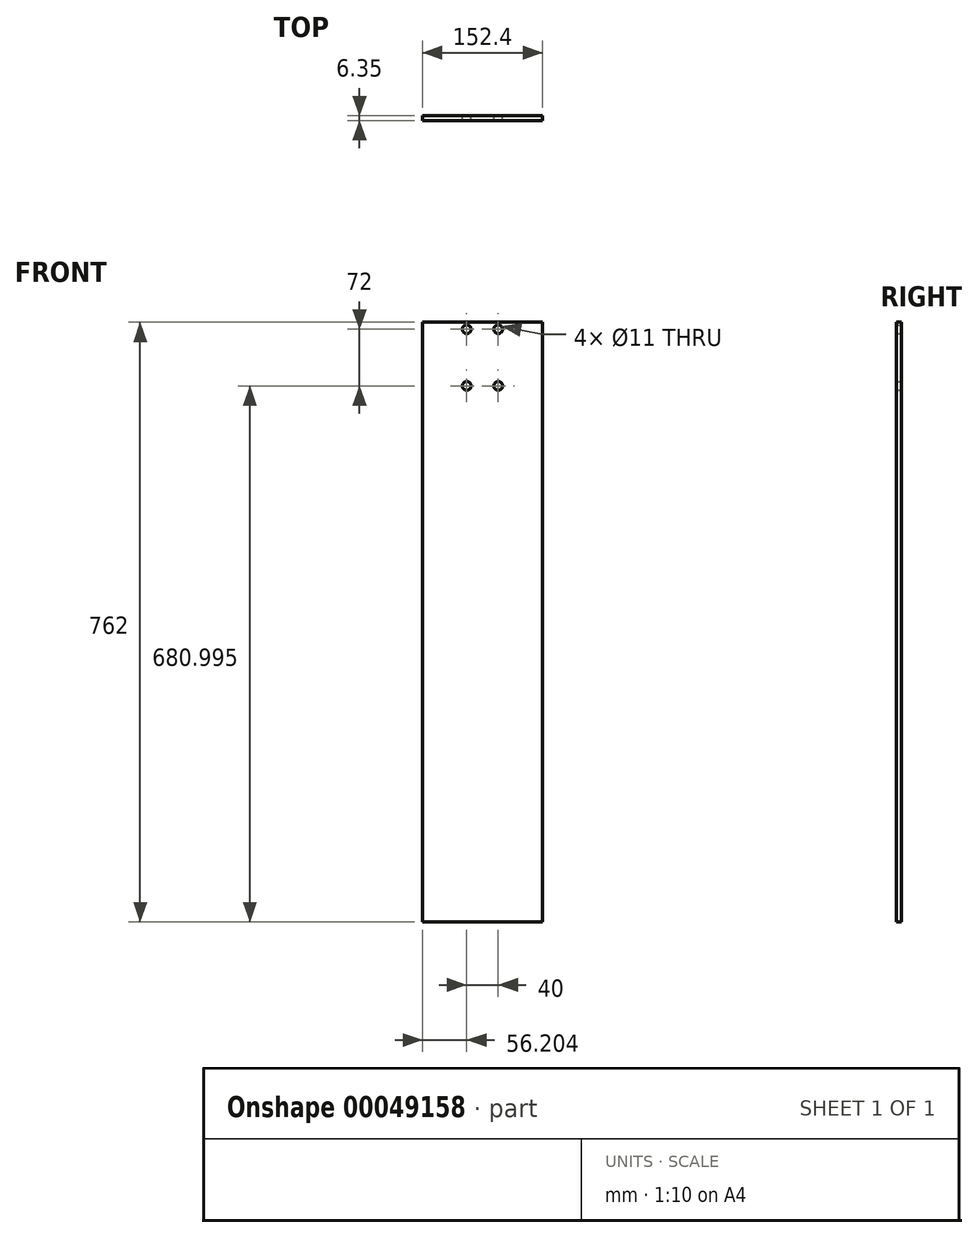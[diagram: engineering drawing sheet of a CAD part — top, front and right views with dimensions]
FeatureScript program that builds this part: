
annotation { "Feature Type Name" : "Feature", "Feature Type Description" : "" }
export const myFeature = defineFeature(function(context is Context, id is Id, definition is map)
    precondition{}
    {
        {
            var Q0;
            Q0=qCreatedBy(makeId("Front.planeOp"),FACE);
            var sketch = newSketch(context, id + "F0", { "sketchPlane" : qUnion([Q0])});
            skLineSegment(sketch, "E0.bottom", {"start": v(-74.92, 649.94) * mm, "end": v(77.48, 649.94) * mm});
            skLineSegment(sketch, "E0.top", {"start": v(-74.92, -112.06) * mm, "end": v(77.48, -112.06) * mm});
            skLineSegment(sketch, "E0.left", {"start": v(-74.92, 649.94) * mm, "end": v(-74.92, -112.06) * mm});
            skLineSegment(sketch, "E0.right", {"start": v(77.48, 649.94) * mm, "end": v(77.48, -112.06) * mm});
            skSolve(sketch);
        }
        {
            var Q0;
            Q0=makeQuery(id+"F0.imprint","IMPRINT",FACE,{"disambiguationData":[TD([[makeQuery(id+"F0.imprint","IMPRINT",EDGE,{"derivedFrom":sQuery(id+"F0.wireOp",EDGE,"E0.bottom")}),-1.0]])]});
            extrude(context, id + "F1", {"entities" : qUnion([Q0]), "depth" : 6.35 * mm});
        }
        {
            var Q0;
            Q0=makeQuery(id+"F1.opExtrude","CAP_FACE",FACE,{"disambiguationData":[OSD([sQuery(id+"F0.wireOp",EDGE,"E0.bottom"),sQuery(id+"F0.wireOp",EDGE,"E0.top"),sQuery(id+"F0.wireOp",EDGE,"E0.left"),sQuery(id+"F0.wireOp",EDGE,"E0.right")])],"isStart":true});
            var sketch = newSketch(context, id + "F2", { "sketchPlane" : qUnion([Q0])});
            skCircle(sketch, "E1", {"center": v(-21.28, 640.94) * mm, "radius": 5.5 * mm});
            skCircle(sketch, "E2", {"center": v(18.72, 640.94) * mm, "radius": 5.5 * mm});
            skCircle(sketch, "E3", {"center": v(-21.28, 568.94) * mm, "radius": 5.5 * mm});
            skCircle(sketch, "E4", {"center": v(18.72, 568.94) * mm, "radius": 5.5 * mm});
            skSolve(sketch);
        }
        {
            var Q0;
            Q0 = qSketchRegion(id + "F2", true);
            extrude(context, id + "F3", {"entities" : qUnion([Q0]), "operationType" : NewBodyOperationType.REMOVE, "endBound" : BoundingType.THROUGH_ALL, "oppositeDirection" : true, "depth" : 25 * mm});
        }
    });
